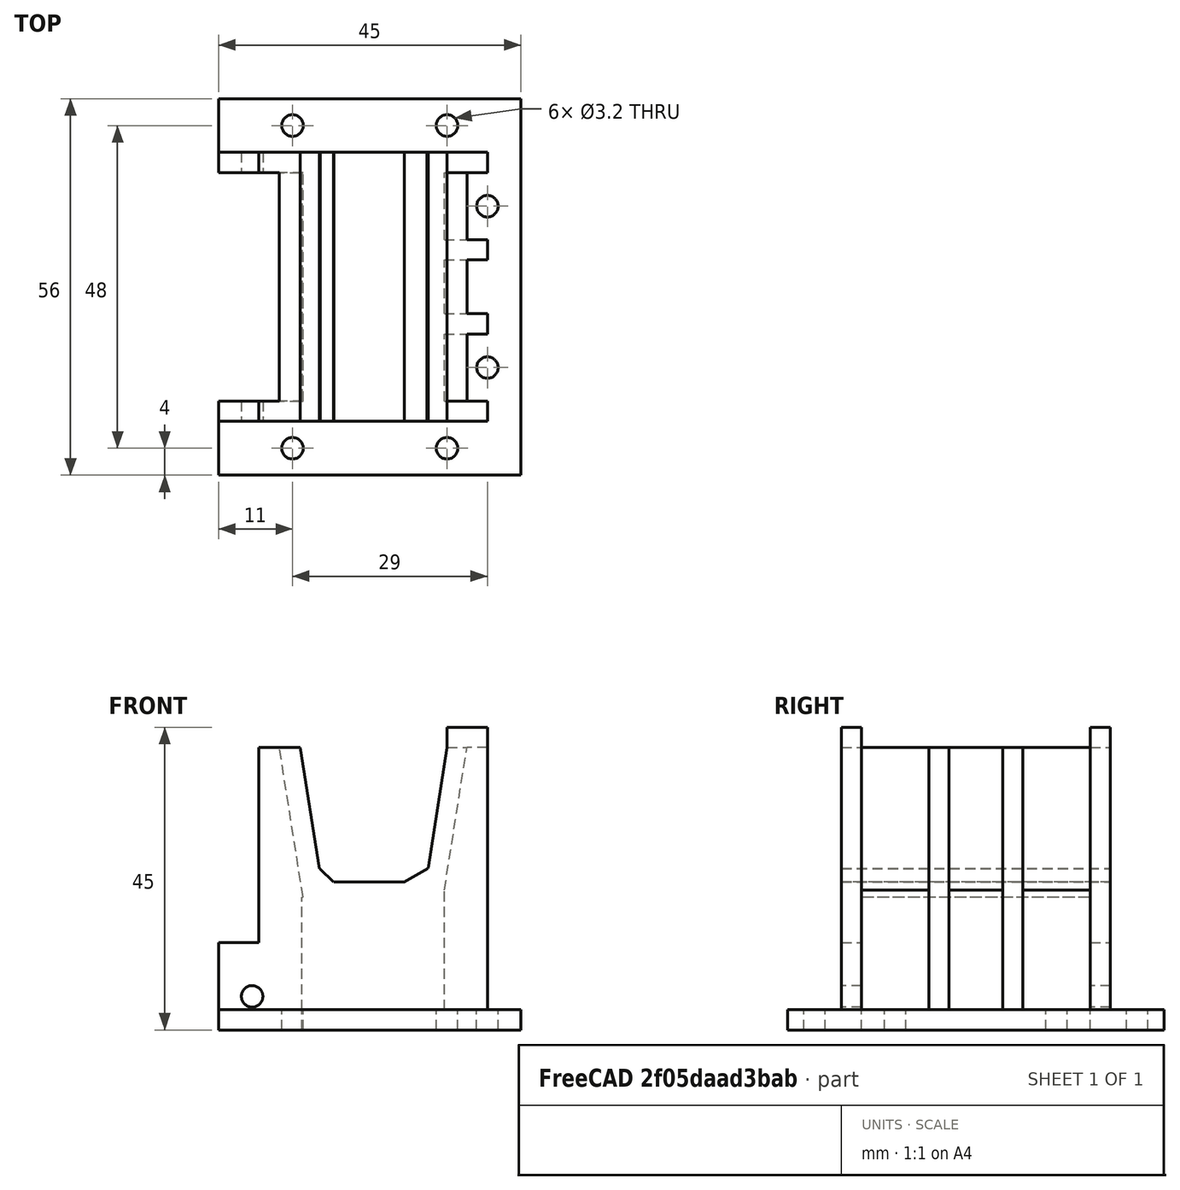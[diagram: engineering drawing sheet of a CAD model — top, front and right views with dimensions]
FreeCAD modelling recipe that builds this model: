
FCSTD DOCUMENT  (FreeCAD 0.16R6707 (Git))
Label: xmaxx-back-bracket2
License: All rights reserved
LicenseURL: http://en.wikipedia.org/wiki/All_rights_reserved
objects: Part::Cut×21, Part::Box×20, Part::Cylinder×7, Part::MultiFuse×3, Part::Fuse×2
note: 53 computed .brp shape members not serialized (recipe doc carries the construction recipe); baked Part::Feature solids carry a one-line shape summary decoded from their .brp

FEATURE [Part::Box] Box  label="Cube"
  Height = 42
  Length = 34
  Width = 40
FEATURE [Part::Box] Box001  label="Cube001"
  Height = 20
  Length = 10.5
  Placement = pos=(11.15,0,22) rot=(0,0,1;0rad)
  Width = 40
FEATURE [Part::Box] Box003  label="Cube003"
  Height = 19
  Length = 7
  Placement = pos=(9,0,24) rot=(0,-1,0;0.15708rad)
  Width = 40
FEATURE [Part::Box] Box004  label="Cube004"
  Height = 19
  Length = 10
  Placement = pos=(15.3,0,25.6) rot=(0,1,0;0.15708rad)
  Width = 40
FEATURE [Part::Box] Box005  label="Cube005"
  Height = 2.8
  Length = 2.8
  Placement = pos=(9.1,0,24) rot=(0,1,0;0.785398rad)
  Width = 40
FEATURE [Part::Box] Box006  label="Cube006"
  Height = 3
  Length = 4
  Placement = pos=(21.6,0,22) rot=(0,-1,0;0.523599rad)
  Width = 40
FEATURE [Part::Cut] Cut
  Base = -> Box
  Tool = -> Box001
FEATURE [Part::Cut] Cut001
  Base = -> Cut
  Tool = -> Box003
FEATURE [Part::Cut] Cut002
  Base = -> Cut001
  Tool = -> Box005
FEATURE [Part::Cut] Cut003
  Base = -> Cut002
  Tool = -> Box004
FEATURE [Part::Cut] Cut004
  Base = -> Cut003
  Tool = -> Box006
FEATURE [Part::Box] Box007  label="Cube007"
  Height = 17.8
  Length = 8.6
  Placement = pos=(-2.19,3,3) rot=(0,0,1;0rad)
  Width = 34
FEATURE [Part::Box] Box008  label="Cube008"
  Height = 23
  Length = 10
  Placement = pos=(-3.3,3,18.2) rot=(0,-1,0;0.15708rad)
  Width = 34
FEATURE [Part::Box] Box011  label="Cube011"
  Height = 17.8
  Length = 8.6
  Placement = pos=(27.6,27,3) rot=(0,0,1;0rad)
  Width = 10
FEATURE [Part::Box] Box012  label="Cube012"
  Height = 17.8
  Length = 8.6
  Placement = pos=(27.6,16,3) rot=(0,0,1;0rad)
  Width = 8
FEATURE [Part::Box] Box013  label="Cube013"
  Height = 17.8
  Length = 8.6
  Placement = pos=(27.6,3,3) rot=(0,0,1;0rad)
  Width = 10
FEATURE [Part::Box] Box016  label="Cube016"
  Height = 23
  Length = 10
  Placement = pos=(27.6,27,20.8) rot=(0,1,0;0.15708rad)
  Width = 10
FEATURE [Part::Cut] Cut005
  Base = -> Cut004
  Tool = -> Box007
FEATURE [Part::Cut] Cut006
  Base = -> Cut005
  Tool = -> Box008
FEATURE [Part::Box] Box017  label="Cube017"
  Height = 23
  Length = 10
  Placement = pos=(27.6,16,20.8) rot=(0,1,0;0.15708rad)
  Width = 8
FEATURE [Part::Box] Box018  label="Cube018"
  Height = 23
  Length = 10
  Placement = pos=(27.6,3,20.8) rot=(0,1,0;0.15708rad)
  Width = 10
FEATURE [Part::Cut] Cut011
  Base = -> Cut006
  Tool = -> Box011
FEATURE [Part::Cut] Cut012
  Base = -> Cut011
  Tool = -> Box016
FEATURE [Part::Cut] Cut013
  Base = -> Cut012
  Tool = -> Box012
FEATURE [Part::Cut] Cut014
  Base = -> Cut013
  Tool = -> Box017
FEATURE [Part::Cut] Cut015
  Base = -> Cut014
  Tool = -> Box013
FEATURE [Part::Cut] Cut016
  Base = -> Cut015
  Tool = -> Box018
FEATURE [Part::Box] Box019  label="Cube019"
  Height = 3
  Length = 45
  Placement = pos=(-6,-8,0) rot=(0,0,1;0rad)
  Width = 56
FEATURE [Part::Fuse] Fusion
  Base = -> Cut016
  Tool = -> Box019
FEATURE [Part::Cylinder] Cylinder002
  Angle = 360
  Height = 10
  Placement = pos=(34,8,0) rot=(0,0,1;0rad)
  Radius = 1.6
FEATURE [Part::Cylinder] Cylinder003
  Angle = 360
  Height = 10
  Placement = pos=(34,32,0) rot=(0,0,1;0rad)
  Radius = 1.6
FEATURE [Part::Cut] Cut019
  Base = -> Fusion
  Tool = -> Cylinder002
FEATURE [Part::Cut] Cut020
  Base = -> Cut019
  Tool = -> Cylinder003
FEATURE [Part::Box] Box020  label="Cube020"
  Height = 3
  Length = 6
  Placement = pos=(28,0,42) rot=(0,0,1;0rad)
  Width = 3
FEATURE [Part::Box] Box021  label="Cube021"
  Height = 3
  Length = 6
  Placement = pos=(28,37,42) rot=(0,0,1;0rad)
  Width = 3
FEATURE [Part::Box] Box022  label="Cube022"
  Height = 3
  Length = 13
  Placement = pos=(-6.6,3,0) rot=(0,0,1;0rad)
  Width = 34
FEATURE [Part::Cut] Cut021
  Base = -> Cut020
  Tool = -> Box022
FEATURE [Part::Box] Box023  label="Cube023"
  Height = 10
  Length = 6
  Placement = pos=(-6,0,3) rot=(0,0,1;0rad)
  Width = 3
FEATURE [Part::Box] Box024  label="Cube024"
  Height = 10
  Length = 6
  Placement = pos=(-6,37,3) rot=(0,0,1;0rad)
  Width = 3
FEATURE [Part::Fuse] Fusion001
  Base = -> Box020
  Tool = -> Cut021
FEATURE [Part::MultiFuse] Fusion002
  Shapes = -> [Fusion001,Box021]
FEATURE [Part::MultiFuse] Fusion003
  Shapes = -> [Fusion002,Box023]
FEATURE [Part::MultiFuse] Fusion004
  Shapes = -> [Fusion003,Box024]
FEATURE [Part::Cylinder] Cylinder
  Angle = 360
  Height = 50
  Placement = pos=(-1,45,5) rot=(1,0,0;1.5708rad)
  Radius = 1.6
FEATURE [Part::Cut] Cut022
  Base = -> Fusion004
  Tool = -> Cylinder
FEATURE [Part::Cylinder] Cylinder004
  Angle = 360
  Height = 10
  Placement = pos=(5,-4,0) rot=(0,0,1;0rad)
  Radius = 1.6
FEATURE [Part::Cylinder] Cylinder005
  Angle = 360
  Height = 10
  Placement = pos=(28,-4,0) rot=(0,0,1;0rad)
  Radius = 1.6
FEATURE [Part::Cylinder] Cylinder006
  Angle = 360
  Height = 10
  Placement = pos=(5,44,0) rot=(0,0,1;0rad)
  Radius = 1.6
FEATURE [Part::Cylinder] Cylinder007
  Angle = 360
  Height = 10
  Placement = pos=(28,44,0) rot=(0,0,1;0rad)
  Radius = 1.6
FEATURE [Part::Cut] Cut023
  Base = -> Cut022
  Tool = -> Cylinder004
FEATURE [Part::Cut] Cut024
  Base = -> Cut023
  Tool = -> Cylinder005
FEATURE [Part::Cut] Cut025
  Base = -> Cut024
  Tool = -> Cylinder006
FEATURE [Part::Cut] Cut026
  Base = -> Cut025
  Tool = -> Cylinder007
